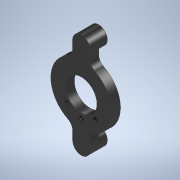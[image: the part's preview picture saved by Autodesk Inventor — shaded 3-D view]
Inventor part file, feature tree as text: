
AUTODESK INVENTOR PART (.ipt)
format: ipt  version: 2020 (Build 240168000, 168)  size: 148,480 bytes
history: native  units: in
note: dims shown in document units (in); Inventor stores cm internally (conversion verified against a paired STEP export)
features: extrude x2, sketch x1, fillet x1
ambient origin geometry x8: Origin, YZ Plane, XZ Plane, XY Plane, X Axis, Y Axis, Z Axis, Center Point
bodies: Solid1 (feature_tree)
feature tree (4):
  sketch  "Sketch1"  dims[d0=0.45in d1=1.25in d2=0.25in d3=0.875in d6=0.065in d7=0.125in d8=0.0in d9=0.125in d10=0.0in d11=0.125in d12=0.58in d13=45.0deg d14=45.0deg]
  extrude  "Extrusion1"  Depth=0.125in
  extrude  "Extrusion2"  Depth=0.25in
  fillet  "Fillet1"  Radius=0.875in
